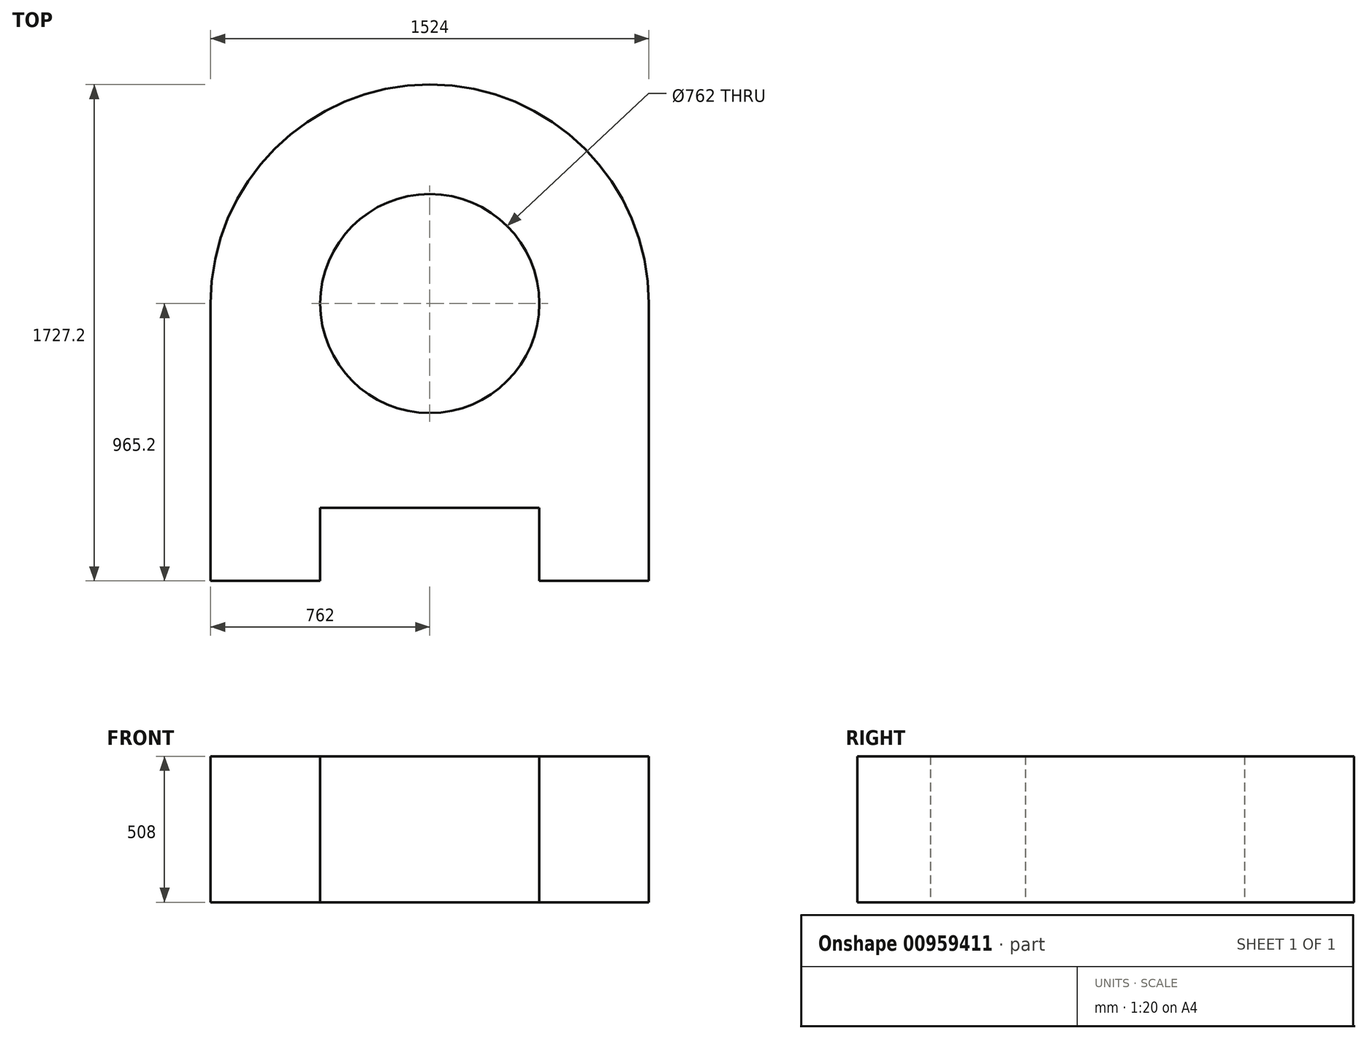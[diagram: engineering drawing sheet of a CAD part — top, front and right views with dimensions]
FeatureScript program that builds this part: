
annotation { "Feature Type Name" : "Feature", "Feature Type Description" : "" }
export const myFeature = defineFeature(function(context is Context, id is Id, definition is map)
    precondition{}
    {
        {
            var Q0;
            Q0=qCreatedBy(makeId("Top.planeOp"),FACE);
            var sketch = newSketch(context, id + "F0", { "sketchPlane" : qUnion([Q0])});
            skCircle(sketch, "E0", {"center": v(0, 0) * mm, "radius": 381 * mm});
            skCircle(sketch, "E1", {"center": v(0, 0) * mm, "radius": 762 * mm});
            skLineSegment(sketch, "E2.bottom", {"start": v(-762, 0) * mm, "end": v(762, 0) * mm});
            skLineSegment(sketch, "E2.top", {"start": v(-762, -965.2) * mm, "end": v(762, -965.2) * mm});
            skLineSegment(sketch, "E2.left", {"start": v(-762, 0) * mm, "end": v(-762, -965.2) * mm});
            skLineSegment(sketch, "E2.right", {"start": v(762, 0) * mm, "end": v(762, -965.2) * mm});
            skLineSegment(sketch, "E3.bottom", {"start": v(-381, -965.2) * mm, "end": v(381, -965.2) * mm});
            skLineSegment(sketch, "E3.top", {"start": v(-381, -711.2) * mm, "end": v(381, -711.2) * mm});
            skLineSegment(sketch, "E3.left", {"start": v(-381, -965.2) * mm, "end": v(-381, -711.2) * mm});
            skLineSegment(sketch, "E3.right", {"start": v(381, -965.2) * mm, "end": v(381, -711.2) * mm});
            skSolve(sketch);
        }
        {
            var Q0;
            {var subQ0=sQuery(id+"F0.wireOp",EDGE,"E2.bottom");var subQ1=sQuery(id+"F0.wireOp",EDGE,"E0");var subQ2=makeQuery(id+"F0.imprint","INTERSECT",VERTEX,{"disambiguationData":[OD(0.0)],"derivedFrom":[subQ1,subQ0]});Q0=makeQuery(id+"F0.imprint","IMPRINT",FACE,{"disambiguationData":[TD([[makeQuery(id+"F0.imprint","IMPRINT",EDGE,{"disambiguationData":[TD([[subQ2,1.0]])],"derivedFrom":subQ1}),-1.0]])]});}
            var Q1;
            {var subQ0=sQuery(id+"F0.wireOp",EDGE,"E2.left");Q1=makeQuery(id+"F0.imprint","IMPRINT",FACE,{"disambiguationData":[TD([[makeQuery(id+"F0.imprint","IMPRINT",EDGE,{"derivedFrom":subQ0}),1.0]])]});}
            var Q2;
            {var subQ4=sQuery(id+"F0.wireOp",EDGE,"E2.right");Q2=makeQuery(id+"F0.imprint","IMPRINT",FACE,{"disambiguationData":[TD([[makeQuery(id+"F0.imprint","IMPRINT",EDGE,{"derivedFrom":subQ4}),-1.0]])]});}
            var Q3;
            {var subQ0=sQuery(id+"F0.wireOp",EDGE,"E2.bottom");var subQ7=sQuery(id+"F0.wireOp",EDGE,"E0");var subQ8=makeQuery(id+"F0.imprint","INTERSECT",VERTEX,{"disambiguationData":[OD(0.0)],"derivedFrom":[subQ7,subQ0]});Q3=makeQuery(id+"F0.imprint","IMPRINT",FACE,{"disambiguationData":[TD([[makeQuery(id+"F0.imprint","IMPRINT",EDGE,{"disambiguationData":[TD([[subQ8,-1.0]])],"derivedFrom":subQ7}),-1.0]])]});}
            extrude(context, id + "F1", {"entities" : qUnion([Q0, Q1, Q2, Q3]), "depth" : 508 * mm, "offsetDistance" : 25.4 * mm});
        }
    });
